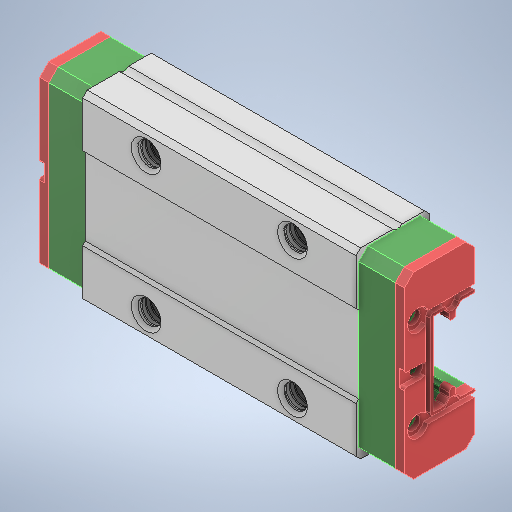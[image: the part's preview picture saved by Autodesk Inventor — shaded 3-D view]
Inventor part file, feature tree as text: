
AUTODESK INVENTOR PART (.ipt)
format: ipt  version: 2025.2 (Build 292293000, 293)  size: 7,672,320 bytes
history: native  units: in
note: dims shown in document units (in); Inventor stores cm internally (conversion verified against a paired STEP export)
features: other x5, plane x1
ambient origin geometry x8: Origin, YZ Plane, XZ Plane, XY Plane, X Axis, Y Axis, Z Axis, Center Point
bodies: Solid1 (feature_tree), Solid2 (feature_tree), Solid3 (feature_tree), Solid4 (feature_tree), Solid5 (feature_tree)
feature tree (6):
  plane  "Work Plane1"
  other  "End Cap 1"
  other  "End Seal 1"
  other  "Block"
  other  "End Cap 2"
  other  "End Seal 2"
